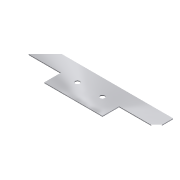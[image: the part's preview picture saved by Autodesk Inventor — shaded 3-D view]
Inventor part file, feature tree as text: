
AUTODESK INVENTOR PART (.ipt)
format: ipt  version: 2016 (Build 200138000, 138)  size: 107,520 bytes
history: native  units: mm
features: sketch x3, extrude x2, other x1, hole x1, mirror x1, projected_geometry x1
ambient origin geometry x8: Origin, YZ Plane, XZ Plane, XY Plane, X Axis, Y Axis, Z Axis, Center Point
bodies: Solid1 (feature_tree)
feature tree (9):
  other  "skeleton.ipt"
  extrude  "Extrusion1"  Depth=300.0mm
  hole  "Hole1"  [1 undecoded]
  extrude  "Extrusion2"  TaperAngle=0.0deg  [1 undecoded]
  mirror  "Mirror1"
  sketch  "Sketch1"  dims[d0=10.0mm d1=300.0mm]
  sketch  "Sketch2"  dims[d2=75.0mm d3=2.0mm d4=0.0mm]
  projected_geometry  "Projected Loop1"
  sketch  "Sketch3"  dims[d5=60.0mm d6=11.0mm d7=6.0mm d8=4.0mm d9=2.0mm d10=90.0deg d11=8.0mm d12=20.594885mm d13=0.0mm d14=75.0mm d15=150.0mm d16=37.5mm d18=0.0mm d19=10.0mm d20=0.0mm]
note: 2 required parameter values undecoded (feature->parameter linkage not recoverable at this tier; creation-order binding heuristic only, values carry confidence <= 0.55)
